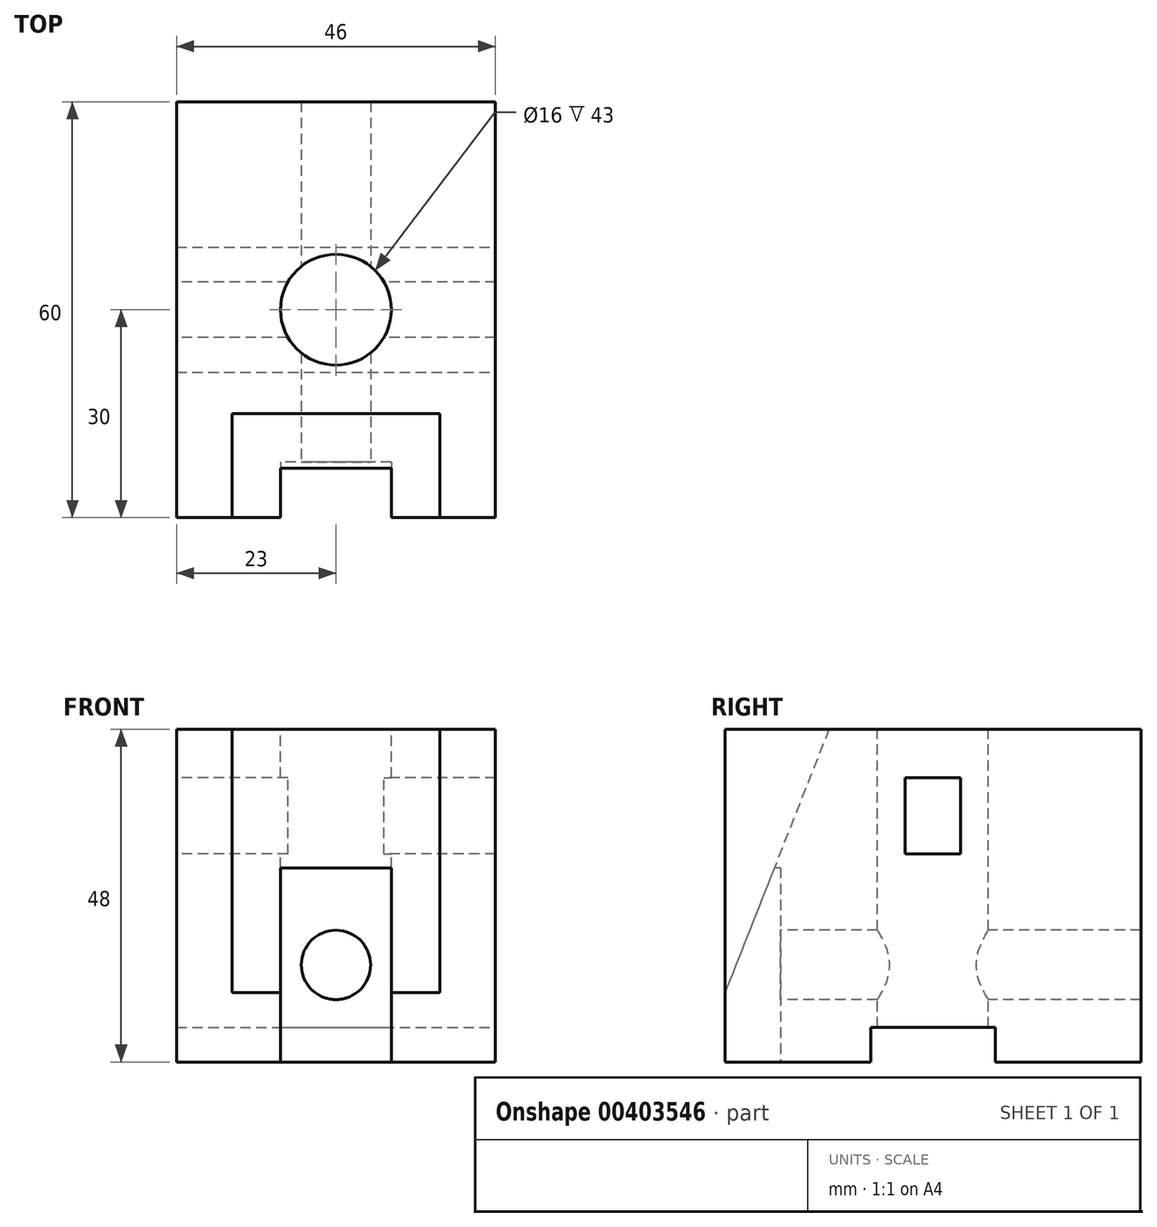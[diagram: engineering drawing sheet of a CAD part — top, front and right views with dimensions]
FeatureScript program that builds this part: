
annotation { "Feature Type Name" : "Feature", "Feature Type Description" : "" }
export const myFeature = defineFeature(function(context is Context, id is Id, definition is map)
    precondition{}
    {
        {
            var Q0;
            Q0=qCreatedBy(makeId("Right.planeOp"),FACE);
            var sketch = newSketch(context, id + "F0", { "sketchPlane" : qUnion([Q0])});
            skLineSegment(sketch, "E0.bottom", {"start": v(-30, 24) * mm, "end": v(30, 24) * mm});
            skLineSegment(sketch, "E0.top", {"start": v(-30, -24) * mm, "end": v(30, -24) * mm});
            skLineSegment(sketch, "E0.left", {"start": v(-30, 24) * mm, "end": v(-30, -24) * mm});
            skLineSegment(sketch, "E0.right", {"start": v(30, 24) * mm, "end": v(30, -24) * mm});
            skPoint(sketch, "E0.middle", {"position": v(0, 0) * mm});
            skLineSegment(sketch, "E1.bottom", {"start": v(4, 6) * mm, "end": v(-4, 6) * mm});
            skLineSegment(sketch, "E1.top", {"start": v(4, 17) * mm, "end": v(-4, 17) * mm});
            skLineSegment(sketch, "E1.left", {"start": v(4, 6) * mm, "end": v(4, 17) * mm});
            skLineSegment(sketch, "E1.right", {"start": v(-4, 6) * mm, "end": v(-4, 17) * mm});
            skPoint(sketch, "E1.middle", {"position": v(0, 11.5) * mm});
            skSolve(sketch);
        }
        {
            var Q0;
            Q0 = qSketchRegion(id + "F0", true);
            extrude(context, id + "F1", {"entities" : qUnion([Q0]), "endBound" : BoundingType.SYMMETRIC, "depth" : 46 * mm});
        }
        {
            var Q0;
            Q0=makeQuery(id+"F1.opExtrude","CAP_FACE",FACE,{"disambiguationData":[OSD([sQuery(id+"F0.wireOp",EDGE,"E0.bottom"),sQuery(id+"F0.wireOp",EDGE,"E0.top"),sQuery(id+"F0.wireOp",EDGE,"E0.left"),sQuery(id+"F0.wireOp",EDGE,"E0.right"),sQuery(id+"F0.wireOp",EDGE,"E1.bottom"),sQuery(id+"F0.wireOp",EDGE,"E1.top"),sQuery(id+"F0.wireOp",EDGE,"E1.left"),sQuery(id+"F0.wireOp",EDGE,"E1.right")])],"isStart":false});
            var sketch = newSketch(context, id + "F2", { "sketchPlane" : qUnion([Q0])});
            skLineSegment(sketch, "E2.bottom", {"start": v(-9, -19) * mm, "end": v(9, -19) * mm});
            skLineSegment(sketch, "E2.top", {"start": v(-9, -24) * mm, "end": v(9, -24) * mm});
            skLineSegment(sketch, "E2.left", {"start": v(-9, -19) * mm, "end": v(-9, -24) * mm});
            skLineSegment(sketch, "E2.right", {"start": v(9, -19) * mm, "end": v(9, -24) * mm});
            skSolve(sketch);
        }
        {
            var Q0;
            Q0 = qSketchRegion(id + "F2", true);
            extrude(context, id + "F3", {"entities" : qUnion([Q0]), "operationType" : NewBodyOperationType.REMOVE, "endBound" : BoundingType.THROUGH_ALL, "oppositeDirection" : true, "depth" : 25 * mm});
        }
        {
            var Q0;
            Q0=qCreatedBy(makeId("Right.planeOp"),FACE);
            var sketch = newSketch(context, id + "F4", { "sketchPlane" : qUnion([Q0])});
            skLineSegment(sketch, "E3", {"start": v(-30, 24) * mm, "end": v(-15, 24) * mm});
            skLineSegment(sketch, "E4", {"start": v(-15, 24) * mm, "end": v(-30, -14) * mm});
            skLineSegment(sketch, "E5", {"start": v(-30, -14) * mm, "end": v(-30, 24) * mm});
            skSolve(sketch);
        }
        {
            var Q0;
            Q0 = qSketchRegion(id + "F4", true);
            extrude(context, id + "F5", {"entities" : qUnion([Q0]), "operationType" : NewBodyOperationType.REMOVE, "endBound" : BoundingType.SYMMETRIC, "oppositeDirection" : true, "depth" : 30 * mm});
        }
        {
            var Q0;
            Q0=makeQuery(id+"F1.opExtrude","SWEPT_FACE",FACE,{"disambiguationData":[OSD([sQuery(id+"F0.wireOp",EDGE,"E0.bottom")])]});
            var sketch = newSketch(context, id + "F6", { "sketchPlane" : qUnion([Q0])});
            skCircle(sketch, "E6", {"center": v(0, 0) * mm, "radius": 8 * mm});
            skSolve(sketch);
        }
        {
            var Q0;
            Q0 = qSketchRegion(id + "F6", true);
            extrude(context, id + "F7", {"entities" : qUnion([Q0]), "operationType" : NewBodyOperationType.REMOVE, "endBound" : BoundingType.THROUGH_ALL, "oppositeDirection" : true, "depth" : 25 * mm});
        }
        {
            var Q0;
            Q0=makeQuery(id+"F1.opExtrude","SWEPT_FACE",FACE,{"disambiguationData":[OSD([sQuery(id+"F0.wireOp",EDGE,"E0.left")])]});
            var sketch = newSketch(context, id + "F8", { "sketchPlane" : qUnion([Q0])});
            skLineSegment(sketch, "E7.bottom", {"start": v(-8, 4) * mm, "end": v(8, 4) * mm});
            skLineSegment(sketch, "E7.top", {"start": v(-8, -24) * mm, "end": v(8, -24) * mm});
            skLineSegment(sketch, "E7.left", {"start": v(-8, 4) * mm, "end": v(-8, -24) * mm});
            skLineSegment(sketch, "E7.right", {"start": v(8, 4) * mm, "end": v(8, -24) * mm});
            skSolve(sketch);
        }
        {
            var Q0;
            Q0 = qSketchRegion(id + "F8", true);
            extrude(context, id + "F9", {"entities" : qUnion([Q0]), "operationType" : NewBodyOperationType.REMOVE, "oppositeDirection" : true, "depth" : 8 * mm});
        }
        {
            var Q0;
            Q0=makeQuery(id+"F9.boolean.opBoolean","COPY",FACE,{"derivedFrom":makeQuery(id+"F9.opExtrude","CAP_FACE",FACE,{"disambiguationData":[OSD([sQuery(id+"F8.wireOp",EDGE,"E7.bottom"),sQuery(id+"F8.wireOp",EDGE,"E7.top"),sQuery(id+"F8.wireOp",EDGE,"E7.left"),sQuery(id+"F8.wireOp",EDGE,"E7.right")])],"isStart":false})});
            var sketch = newSketch(context, id + "F10", { "sketchPlane" : qUnion([Q0])});
            skCircle(sketch, "E8", {"center": v(0, -10) * mm, "radius": 5 * mm});
            skSolve(sketch);
        }
        {
            var Q0;
            Q0 = qSketchRegion(id + "F10", true);
            extrude(context, id + "F11", {"entities" : qUnion([Q0]), "operationType" : NewBodyOperationType.REMOVE, "endBound" : BoundingType.THROUGH_ALL, "oppositeDirection" : true, "depth" : 25 * mm});
        }
    });
